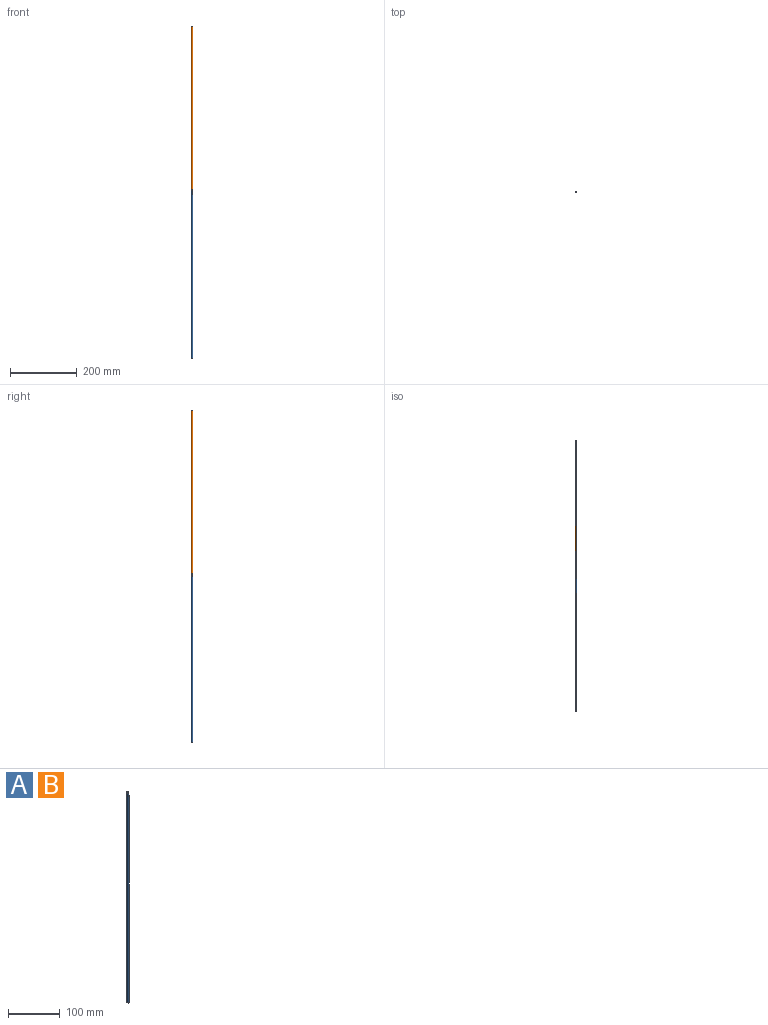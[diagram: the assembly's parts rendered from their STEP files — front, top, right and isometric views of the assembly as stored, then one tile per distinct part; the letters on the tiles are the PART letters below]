
ASSEMBLY  parts=2 mates=1
PART A: 6 faces, bbox 4x4x500 mm
  f0: plane 4x2mm, normal (0,0,1), area 6.3mm2, adj f1,f3
  f1: cylinder r=2mm len=500mm, axis (0,0,-1), area 6217.1mm2, adj f0,f2,f3,f4,f5
  f2: plane 4x4mm, normal (0,0,-1), area 12.6mm2, adj f1
  f3: plane 10x4mm, normal (1,0,0), area 36.9mm2, adj f0,f1,f4,f5
  f4: plane 4x2mm, normal (0,0,1), area 6.3mm2, adj f1,f3
  f5: cylinder r=1mm len=2mm, axis (1,0,0), area 11.7mm2, adj f1,f3
PART B: same geometry as A
PLACE A t=(-70.84,7.98,-176.69)mm
PLACE B rot(axis=(0,1,0),180deg) t=(-70.84,7.98,817.31)mm
MATE revolute B.f5 <-> A.f5  axis (-1,0,0) through (-70.84,7.98,320.31)mm
